# Revit family: NLRS_57_AIR_UN_door-wall grill wgzc overflow LT_sacs
name_source: partatom
category: Air Terminals
revit_build: Autodesk Revit 2018 (Build: 20190510_1515(x64)
units: mm (PartAtom-declared; Revit-internal decimal feet)

## family parameters
Always vertical = No
Cut with Voids When Loaded = Yes
OmniClass Number = 23.75.70.21.27.11
OmniClass Title = Diffusers, Registers, and Grilles
Part Type = Normal
Room Calculation Point = Yes
Round Connector Dimension = Use Diameter
Shared = No
Work Plane-Based = No

## types (1)
- WGZC
    Assembly Code = 57.0
    Description = Solid Air wall/door grill WGZC (overflow)
    FactorTable = WGZ_factors
    FireRating = 0
    IfcDescription = Solid Air wall/door grill WGZC (overflow)
    IfcExportAs = IfcAirTerminal
    IfcExportType = OVERFLOW
    IsExternal = No
    LoadBearing = No
    LookupTable = WGZC
    Manufacturer = Solid Air Climate Systems
    Max Flow = 0.0 m³/h
    Min Flow = 0.0 m³/h
    Model = Wall/door grill
    NLRS_C_content_datum_uitgifte = 17-08-2021
    NLRS_C_content_provider = Solid Air Climate Solutions
    NLRS_C_content_versie = 3.18.01
    NLRS_C_niveau ontwikkeling = LOD 400
    SACS_Material_Core = Galvanized steel
    SACS_Material_Frame = Extruded Aluminium
    SACS_Show_Symbol = No
    Sound_Table = WGZ_Sound
    URL = https://solid-air.nl

## geometry (parser evidence)
native form markers: Sweep x11
no freeform markers — native parametric forms only
